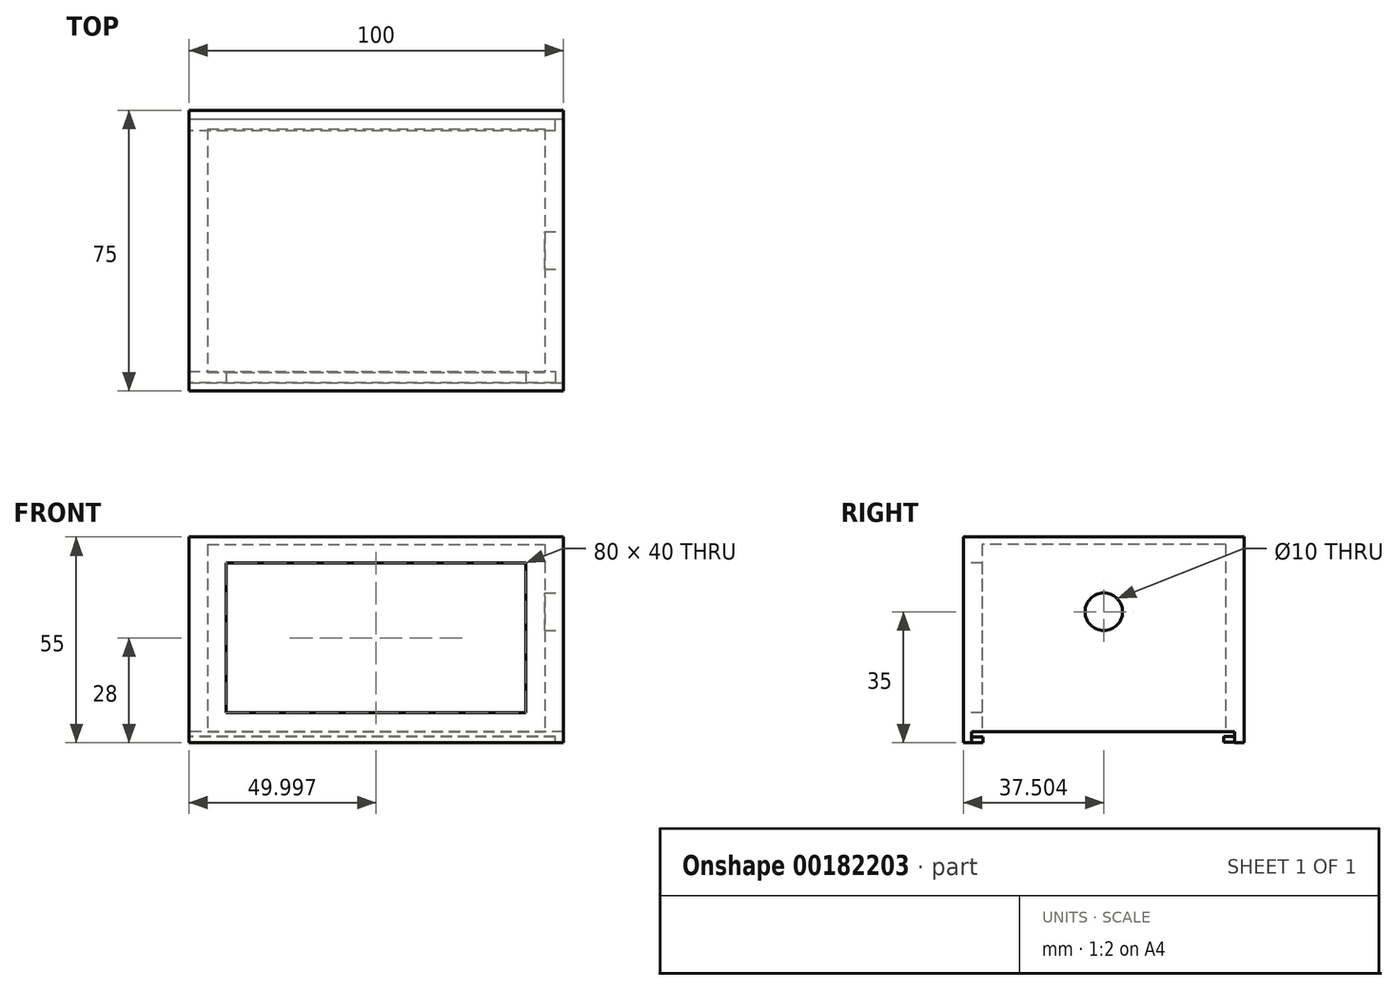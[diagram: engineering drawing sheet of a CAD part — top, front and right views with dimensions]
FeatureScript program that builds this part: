
annotation { "Feature Type Name" : "Feature", "Feature Type Description" : "" }
export const myFeature = defineFeature(function(context is Context, id is Id, definition is map)
    precondition{}
    {
        {
            var Q0;
            Q0=qCreatedBy(makeId("Top.planeOp"),FACE);
            var sketch = newSketch(context, id + "F0", { "sketchPlane" : qUnion([Q0])});
            skLineSegment(sketch, "E0.bottom", {"start": v(-43.25, 42) * mm, "end": v(56.75, 42) * mm});
            skLineSegment(sketch, "E0.top", {"start": v(-43.25, -33) * mm, "end": v(56.75, -33) * mm});
            skLineSegment(sketch, "E0.left", {"start": v(-43.25, 42) * mm, "end": v(-43.25, -33) * mm});
            skLineSegment(sketch, "E0.right", {"start": v(56.75, 42) * mm, "end": v(56.75, -33) * mm});
            skLineSegment(sketch, "E1.bottom", {"start": v(-38.25, 37) * mm, "end": v(51.75, 37) * mm});
            skLineSegment(sketch, "E1.top", {"start": v(-38.25, -28) * mm, "end": v(51.75, -28) * mm});
            skLineSegment(sketch, "E1.left", {"start": v(-38.25, 37) * mm, "end": v(-38.25, -28) * mm});
            skLineSegment(sketch, "E1.right", {"start": v(51.75, 37) * mm, "end": v(51.75, -28) * mm});
            skSolve(sketch);
        }
        {
            var Q0;
            Q0=makeQuery(id+"F0.imprint","IMPRINT",FACE,{"disambiguationData":[TD([[makeQuery(id+"F0.imprint","IMPRINT",EDGE,{"derivedFrom":sQuery(id+"F0.wireOp",EDGE,"E0.bottom")}),-1.0]])]});
            extrude(context, id + "F1", {"entities" : qUnion([Q0]), "depth" : 50 * mm});
        }
        {
            var Q0;
            Q0=makeQuery(id+"F1.opExtrude","CAP_FACE",FACE,{"disambiguationData":[OSD([sQuery(id+"F0.wireOp",EDGE,"E0.bottom"),sQuery(id+"F0.wireOp",EDGE,"E0.top"),sQuery(id+"F0.wireOp",EDGE,"E0.left"),sQuery(id+"F0.wireOp",EDGE,"E0.right"),sQuery(id+"F0.wireOp",EDGE,"E1.bottom"),sQuery(id+"F0.wireOp",EDGE,"E1.top"),sQuery(id+"F0.wireOp",EDGE,"E1.left"),sQuery(id+"F0.wireOp",EDGE,"E1.right")])],"isStart":true});
            var sketch = newSketch(context, id + "F2", { "sketchPlane" : qUnion([Q0])});
            skLineSegment(sketch, "E2.bottom", {"start": v(-43.25, 33) * mm, "end": v(56.75, 33) * mm});
            skLineSegment(sketch, "E2.top", {"start": v(-43.25, 30.81) * mm, "end": v(56.75, 30.81) * mm});
            skLineSegment(sketch, "E2.left", {"start": v(-43.25, 33) * mm, "end": v(-43.25, 30.81) * mm});
            skLineSegment(sketch, "E2.right", {"start": v(56.75, 33) * mm, "end": v(56.75, 30.81) * mm});
            skLineSegment(sketch, "E3.bottom", {"start": v(56.75, -42) * mm, "end": v(-43.25, -42) * mm});
            skLineSegment(sketch, "E3.top", {"start": v(56.75, -39.48) * mm, "end": v(-43.25, -39.48) * mm});
            skLineSegment(sketch, "E3.left", {"start": v(56.75, -42) * mm, "end": v(56.75, -39.48) * mm});
            skLineSegment(sketch, "E3.right", {"start": v(-43.25, -42) * mm, "end": v(-43.25, -39.48) * mm});
            skLineSegment(sketch, "E4.bottom", {"start": v(56.75, 30.81) * mm, "end": v(54.58, 30.81) * mm});
            skLineSegment(sketch, "E4.top", {"start": v(56.75, -39.48) * mm, "end": v(54.58, -39.48) * mm});
            skLineSegment(sketch, "E4.left", {"start": v(56.75, 30.81) * mm, "end": v(56.75, -39.48) * mm});
            skLineSegment(sketch, "E4.right", {"start": v(54.58, 30.81) * mm, "end": v(54.58, -39.48) * mm});
            skSolve(sketch);
        }
        {
            var Q0;
            Q0=makeQuery(id+"F2.imprint","IMPRINT",FACE,{"disambiguationData":[TD([[makeQuery(id+"F2.imprint","IMPRINT",EDGE,{"derivedFrom":sQuery(id+"F2.wireOp",EDGE,"E2.bottom")}),-1.0]])]});
            var Q1;
            Q1=makeQuery(id+"F2.imprint","IMPRINT",FACE,{"disambiguationData":[TD([[makeQuery(id+"F2.imprint","IMPRINT",EDGE,{"derivedFrom":sQuery(id+"F2.wireOp",EDGE,"E4.bottom")}),1.0]])]});
            var Q2;
            Q2=makeQuery(id+"F2.imprint","IMPRINT",FACE,{"disambiguationData":[TD([[makeQuery(id+"F2.imprint","IMPRINT",EDGE,{"derivedFrom":sQuery(id+"F2.wireOp",EDGE,"E3.bottom")}),1.0]])]});
            extrude(context, id + "F3", {"entities" : qUnion([Q0, Q1, Q2]), "operationType" : NewBodyOperationType.ADD, "depth" : 3 * mm});
        }
        {
            var Q0;
            Q0=makeQuery(id+"F3.opExtrude","SWEPT_FACE",FACE,{"disambiguationData":[OSD([sQuery(id+"F2.wireOp",EDGE,"E3.top")])]});
            var sketch = newSketch(context, id + "F4", { "sketchPlane" : qUnion([Q0])});
            skSolve(sketch);
        }
        {
            var Q0;
            Q0=makeQuery(id+"F3.opExtrude","SWEPT_FACE",FACE,{"disambiguationData":[OSD([sQuery(id+"F2.wireOp",EDGE,"E2.top")])]});
            var sketch = newSketch(context, id + "F5", { "sketchPlane" : qUnion([Q0])});
            skLineSegment(sketch, "E5.bottom", {"start": v(-54.58, -3) * mm, "end": v(43.25, -3) * mm});
            skLineSegment(sketch, "E5.top", {"start": v(-54.58, -1.5) * mm, "end": v(43.25, -1.5) * mm});
            skLineSegment(sketch, "E5.left", {"start": v(-54.58, -3) * mm, "end": v(-54.58, -1.5) * mm});
            skLineSegment(sketch, "E5.right", {"start": v(43.25, -3) * mm, "end": v(43.25, -1.5) * mm});
            skSolve(sketch);
        }
        {
            var Q0;
            Q0=makeQuery(id+"F5.imprint","IMPRINT",FACE,{"disambiguationData":[TD([[makeQuery(id+"F5.imprint","IMPRINT",EDGE,{"derivedFrom":sQuery(id+"F5.wireOp",EDGE,"E5.bottom")}),-1.0]])]});
            extrude(context, id + "F6", {"entities" : qUnion([Q0]), "operationType" : NewBodyOperationType.ADD, "depth" : 3 * mm});
        }
        {
            var Q0;
            {var subQ0=sQuery(id+"F2.wireOp",EDGE,"E3.top");Q0=makeQuery(id+"F4.imprint","IMPRINT",FACE,{"disambiguationData":[TD([[makeQuery(id+"F4.imprint","IMPRINT",EDGE,{"derivedFrom":makeQuery(id+"F3.opExtrude","CAP_EDGE",EDGE,{"disambiguationData":[OSD([subQ0])],"isStart":false})}),-1.0]])]});}
            var sketch = newSketch(context, id + "F7", { "sketchPlane" : qUnion([Q0])});
            skLineSegment(sketch, "E6.bottom", {"start": v(54.58, -2.81) * mm, "end": v(-43.25, -2.81) * mm});
            skLineSegment(sketch, "E6.top", {"start": v(54.58, -1.31) * mm, "end": v(-43.25, -1.31) * mm});
            skLineSegment(sketch, "E6.left", {"start": v(54.58, -2.81) * mm, "end": v(54.58, -1.31) * mm});
            skLineSegment(sketch, "E6.right", {"start": v(-43.25, -2.81) * mm, "end": v(-43.25, -1.31) * mm});
            skSolve(sketch);
        }
        {
            var Q0;
            Q0 = qSketchRegion(id + "F7", true);
            extrude(context, id + "F8", {"entities" : qUnion([Q0]), "operationType" : NewBodyOperationType.ADD, "depth" : 3 * mm});
        }
        {
            var Q0;
            Q0=makeQuery(id+"F1.opExtrude","CAP_FACE",FACE,{"disambiguationData":[OSD([sQuery(id+"F0.wireOp",EDGE,"E0.bottom"),sQuery(id+"F0.wireOp",EDGE,"E0.top"),sQuery(id+"F0.wireOp",EDGE,"E0.left"),sQuery(id+"F0.wireOp",EDGE,"E0.right"),sQuery(id+"F0.wireOp",EDGE,"E1.bottom"),sQuery(id+"F0.wireOp",EDGE,"E1.top"),sQuery(id+"F0.wireOp",EDGE,"E1.left"),sQuery(id+"F0.wireOp",EDGE,"E1.right")])],"isStart":false});
            var sketch = newSketch(context, id + "F9", { "sketchPlane" : qUnion([Q0])});
            skLineSegment(sketch, "E7.bottom", {"start": v(-43.25, 42) * mm, "end": v(56.75, 42) * mm});
            skLineSegment(sketch, "E7.top", {"start": v(-43.25, -33) * mm, "end": v(56.75, -33) * mm});
            skLineSegment(sketch, "E7.left", {"start": v(-43.25, 42) * mm, "end": v(-43.25, -33) * mm});
            skLineSegment(sketch, "E7.right", {"start": v(56.75, 42) * mm, "end": v(56.75, -33) * mm});
            skSolve(sketch);
        }
        {
            var Q0;
            Q0=makeQuery(id+"F9.imprint","IMPRINT",FACE,{"disambiguationData":[TD([[makeQuery(id+"F9.imprint","IMPRINT",EDGE,{"derivedFrom":sQuery(id+"F9.wireOp",EDGE,"E7.bottom")}),-1.0]])]});
            var Q1;
            Q1=makeQuery(id+"F9.imprint","IMPRINT",FACE,{"disambiguationData":[TD([[makeQuery(id+"F9.imprint","IMPRINT",EDGE,{"derivedFrom":makeQuery(id+"F1.opExtrude","CAP_EDGE",EDGE,{"disambiguationData":[OSD([sQuery(id+"F0.wireOp",EDGE,"E1.bottom")])],"isStart":false})}),-1.0]])]});
            extrude(context, id + "F10", {"entities" : qUnion([Q0, Q1]), "operationType" : NewBodyOperationType.ADD, "depth" : 2 * mm});
        }
        {
            var Q0;
            Q0=makeQuery(id+"F10.boolean.opBoolean","MERGE",FACE,{"derivedFrom":[makeQuery(id+"F3.boolean.opBoolean","MERGE",FACE,{"derivedFrom":[makeQuery(id+"F1.opExtrude","SWEPT_FACE",FACE,{"disambiguationData":[OSD([sQuery(id+"F0.wireOp",EDGE,"E0.top")])]}),makeQuery(id+"F3.opExtrude","SWEPT_FACE",FACE,{"disambiguationData":[OSD([sQuery(id+"F2.wireOp",EDGE,"E2.bottom")])]})]}),makeQuery(id+"F10.opExtrude","SWEPT_FACE",FACE,{"disambiguationData":[OSD([sQuery(id+"F9.wireOp",EDGE,"E7.top")])]})]});
            var sketch = newSketch(context, id + "F11", { "sketchPlane" : qUnion([Q0])});
            skLineSegment(sketch, "E8.bottom", {"start": v(46.75, 5) * mm, "end": v(-33.25, 5) * mm});
            skLineSegment(sketch, "E8.top", {"start": v(46.75, 45) * mm, "end": v(-33.25, 45) * mm});
            skLineSegment(sketch, "E8.left", {"start": v(46.75, 5) * mm, "end": v(46.75, 45) * mm});
            skLineSegment(sketch, "E8.right", {"start": v(-33.25, 5) * mm, "end": v(-33.25, 45) * mm});
            skSolve(sketch);
        }
        {
            var Q0;
            Q0=makeQuery(id+"F11.imprint","IMPRINT",FACE,{"disambiguationData":[TD([[makeQuery(id+"F11.imprint","IMPRINT",EDGE,{"derivedFrom":sQuery(id+"F11.wireOp",EDGE,"E8.bottom")}),-1.0]])]});
            extrude(context, id + "F12", {"entities" : qUnion([Q0]), "operationType" : NewBodyOperationType.REMOVE, "oppositeDirection" : true, "depth" : 25 * mm});
        }
        {
            var Q0;
            Q0=makeQuery(id+"F10.boolean.opBoolean","MERGE",FACE,{"derivedFrom":[makeQuery(id+"F3.boolean.opBoolean","MERGE",FACE,{"derivedFrom":[makeQuery(id+"F1.opExtrude","SWEPT_FACE",FACE,{"disambiguationData":[OSD([sQuery(id+"F0.wireOp",EDGE,"E0.right")])]}),makeQuery(id+"F3.opExtrude","SWEPT_FACE",FACE,{"disambiguationData":[OSD([sQuery(id+"F2.wireOp",EDGE,"E2.right"),sQuery(id+"F2.wireOp",EDGE,"E3.left"),sQuery(id+"F2.wireOp",EDGE,"E4.left")])]})]}),makeQuery(id+"F10.opExtrude","SWEPT_FACE",FACE,{"disambiguationData":[OSD([sQuery(id+"F9.wireOp",EDGE,"E7.right")])]})]});
            var sketch = newSketch(context, id + "F13", { "sketchPlane" : qUnion([Q0])});
            skCircle(sketch, "E9", {"center": v(4.5, 32) * mm, "radius": 5 * mm});
            skSolve(sketch);
        }
        {
            var Q0;
            Q0=makeQuery(id+"F13.imprint","IMPRINT",FACE,{"disambiguationData":[TD([[makeQuery(id+"F13.imprint","IMPRINT",EDGE,{"derivedFrom":sQuery(id+"F13.wireOp",EDGE,"E9")}),1.0]])]});
            extrude(context, id + "F14", {"entities" : qUnion([Q0]), "operationType" : NewBodyOperationType.REMOVE, "oppositeDirection" : true, "depth" : 25 * mm});
        }
    });
